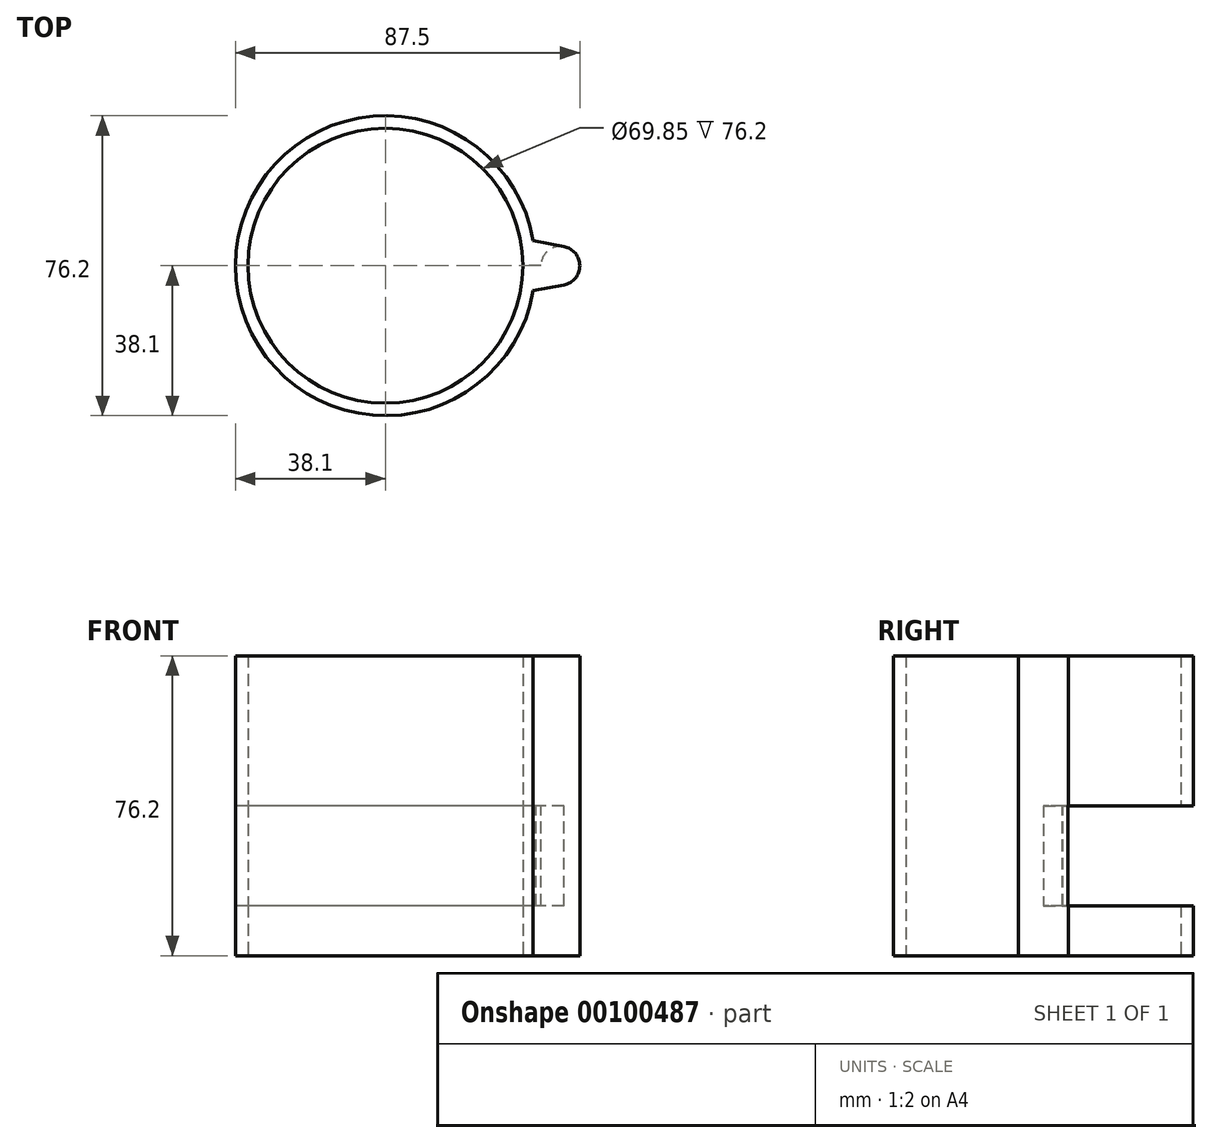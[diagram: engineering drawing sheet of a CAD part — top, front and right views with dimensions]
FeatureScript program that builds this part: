
annotation { "Feature Type Name" : "Feature", "Feature Type Description" : "" }
export const myFeature = defineFeature(function(context is Context, id is Id, definition is map)
    precondition{}
    {
        {
            var Q0;
            Q0=qCreatedBy(makeId("Top.planeOp"),FACE);
            var sketch = newSketch(context, id + "F0", { "sketchPlane" : qUnion([Q0])});
            skCircle(sketch, "E0", {"center": v(0, 0) * mm, "radius": 38.1 * mm});
            skCircle(sketch, "E1", {"center": v(0, 0) * mm, "radius": 34.93 * mm});
            skArc(sketch, "E2", {"start": v(45.37, -4.87) * mm, "mid": v(49.4, 0) * mm, "end": v(45.37, 4.87) * mm});
            skLineSegment(sketch, "E3", {"start": v(45.37, 4.87) * mm, "end": v(37.57, 6.35) * mm});
            skLineSegment(sketch, "E4", {"start": v(45.37, -4.87) * mm, "end": v(37.57, -6.35) * mm});
            skLineSegment(sketch, "E5", {"start": v(-59.15, 0) * mm, "end": v(72.36, 0) * mm, "construction": true});
            skCircle(sketch, "E6", {"center": v(44.45, 0) * mm, "radius": 4.95 * mm});
            skSolve(sketch);
        }
        {
            var Q0;
            Q0=makeQuery(id+"F0.imprint","IMPRINT",FACE,{"disambiguationData":[TD([[makeQuery(id+"F0.imprint","IMPRINT",EDGE,{"derivedFrom":sQuery(id+"F0.wireOp",EDGE,"E1")}),-1.0]])]});
            extrude(context, id + "F1", {"entities" : qUnion([Q0]), "endBound" : BoundingType.SYMMETRIC, "depth" : 76.2 * mm});
        }
        {
            var Q0;
            {var subQ0=sQuery(id+"F0.wireOp",EDGE,"E3");Q0=makeQuery(id+"F0.imprint","IMPRINT",FACE,{"disambiguationData":[TD([[makeQuery(id+"F0.imprint","IMPRINT",EDGE,{"derivedFrom":subQ0}),1.0]])]});}
            var Q1;
            {var subQ0=sQuery(id+"F0.wireOp",EDGE,"E6");var subQ1=makeQuery(id+"F0.imprint","INTERSECT",VERTEX,{"derivedFrom":[sQuery(id+"F0.wireOp",EDGE,"E3"),subQ0]});Q1=makeQuery(id+"F0.imprint","IMPRINT",FACE,{"disambiguationData":[TD([[makeQuery(id+"F0.imprint","IMPRINT",EDGE,{"disambiguationData":[TD([[subQ1,-1.0]])],"derivedFrom":subQ0}),1.0]])]});}
            extrude(context, id + "F2", {"entities" : qUnion([Q0, Q1]), "operationType" : NewBodyOperationType.ADD, "endBound" : BoundingType.SYMMETRIC, "depth" : 76.2 * mm});
        }
        {
            var Q0;
            Q0=qCreatedBy(makeId("Top.planeOp"),FACE);
            var sketch = newSketch(context, id + "F3", { "sketchPlane" : qUnion([Q0])});
            skLineSegment(sketch, "E7.bottom", {"start": v(39.5, 0) * mm, "end": v(-42.95, 0) * mm});
            skLineSegment(sketch, "E7.top", {"start": v(38.25, 40.88) * mm, "end": v(-42.95, 40.88) * mm});
            skLineSegment(sketch, "E7.left", {"start": v(38.25, 6.17) * mm, "end": v(38.25, 40.88) * mm});
            skLineSegment(sketch, "E7.right", {"start": v(-42.95, 0) * mm, "end": v(-42.95, 40.88) * mm});
            skArc(sketch, "E8", {"start": v(45.4, 4.84) * mm, "mid": v(41.33, 3.8) * mm, "end": v(39.5, 0) * mm});
            skLineSegment(sketch, "E9", {"start": v(45.4, 4.84) * mm, "end": v(38.25, 6.17) * mm});
            skPoint(sketch, "E10.orphan", {"position": v(38.25, 0) * mm});
            skSolve(sketch);
        }
        {
            var Q0;
            Q0 = qSketchRegion(id + "F3", true);
            extrude(context, id + "F4", {"entities" : qUnion([Q0]), "operationType" : NewBodyOperationType.REMOVE, "oppositeDirection" : true, "depth" : 25.4 * mm});
        }
    });
